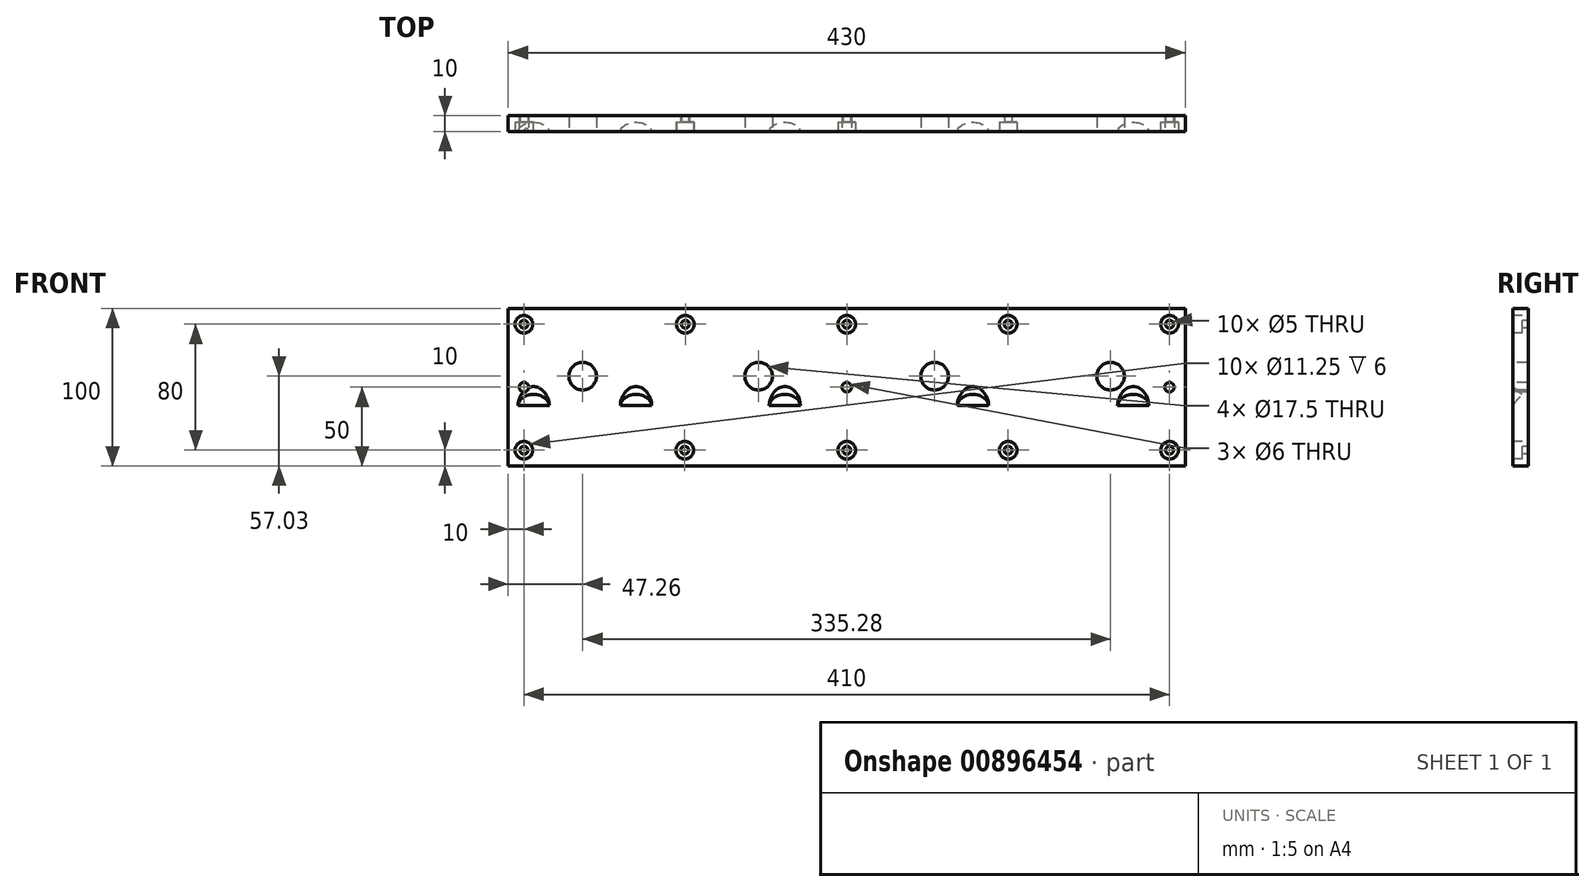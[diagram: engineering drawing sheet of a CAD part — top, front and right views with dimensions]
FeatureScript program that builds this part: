
annotation { "Feature Type Name" : "Feature", "Feature Type Description" : "" }
export const myFeature = defineFeature(function(context is Context, id is Id, definition is map)
    precondition{}
    {
        {
            var Q0;
            Q0=qCreatedBy(makeId("Front.planeOp"),FACE);
            var sketch = newSketch(context, id + "F0", { "sketchPlane" : qUnion([Q0])});
            skLineSegment(sketch, "E0.bottom", {"start": v(0, 0) * mm, "end": v(430, 0) * mm});
            skLineSegment(sketch, "E0.top", {"start": v(0, 100) * mm, "end": v(430, 100) * mm});
            skLineSegment(sketch, "E0.left", {"start": v(0, 0) * mm, "end": v(0, 100) * mm});
            skLineSegment(sketch, "E0.right", {"start": v(430, 0) * mm, "end": v(430, 100) * mm});
            skSolve(sketch);
        }
        {
            var Q0;
            Q0=makeQuery(id+"F0.imprint","IMPRINT",FACE,{"disambiguationData":[TD([[makeQuery(id+"F0.imprint","IMPRINT",EDGE,{"derivedFrom":sQuery(id+"F0.wireOp",EDGE,"E0.bottom")}),1.0]])]});
            extrude(context, id + "F1", {"entities" : qUnion([Q0]), "depth" : 10 * mm, "offsetDistance" : 25 * mm});
        }
        {
            var Q0;
            Q0=makeQuery(id+"F1.opExtrude","CAP_FACE",FACE,{"disambiguationData":[OSD([sQuery(id+"F0.wireOp",EDGE,"E0.bottom"),sQuery(id+"F0.wireOp",EDGE,"E0.top"),sQuery(id+"F0.wireOp",EDGE,"E0.left"),sQuery(id+"F0.wireOp",EDGE,"E0.right")])],"isStart":false});
            var sketch = newSketch(context, id + "F2", { "sketchPlane" : qUnion([Q0])});
            skPoint(sketch, "E1", {"position": v(47.26, 57.03) * mm});
            skPoint(sketch, "E2", {"position": v(159.02, 57.03) * mm});
            skPoint(sketch, "E3", {"position": v(270.78, 57.03) * mm});
            skPoint(sketch, "E4", {"position": v(382.54, 57.03) * mm});
            skPoint(sketch, "E5", {"position": v(10, 10) * mm});
            skPoint(sketch, "E6", {"position": v(112.05, 10) * mm});
            skPoint(sketch, "E7", {"position": v(215, 10) * mm});
            skPoint(sketch, "E8", {"position": v(317.5, 10) * mm});
            skPoint(sketch, "E9", {"position": v(10, 90) * mm});
            skPoint(sketch, "E10", {"position": v(112.5, 90) * mm});
            skPoint(sketch, "E11", {"position": v(215, 90) * mm});
            skPoint(sketch, "E12", {"position": v(317.5, 90) * mm});
            skPoint(sketch, "E13", {"position": v(420, 90) * mm});
            skPoint(sketch, "E14", {"position": v(420, 10) * mm});
            skPoint(sketch, "E15.positionSnap0", {"position": v(0, 50) * mm});
            skPoint(sketch, "E16", {"position": v(215, 50) * mm});
            skPoint(sketch, "E17", {"position": v(420, 50) * mm});
            skPoint(sketch, "E18", {"position": v(10, 50) * mm});
            skSolve(sketch);
        }
        {
            var Q0;
            Q0=sQuery(id+"F2.wireOp",VERTEX,"E1");
            var Q1;
            Q1=sQuery(id+"F2.wireOp",VERTEX,"E2");
            var Q2;
            Q2=sQuery(id+"F2.wireOp",VERTEX,"E3");
            var Q3;
            Q3=sQuery(id+"F2.wireOp",VERTEX,"E4");
            var Q4;
            Q4=makeQuery(id+"F1.opExtrude","SWEPT_BODY",BODY,{"disambiguationData":[OSD([sQuery(id+"F0.wireOp",EDGE,"E0.bottom"),sQuery(id+"F0.wireOp",EDGE,"E0.top"),sQuery(id+"F0.wireOp",EDGE,"E0.left"),sQuery(id+"F0.wireOp",EDGE,"E0.right")])]});
            hole(context, id + "F3", {"style" : HoleStyle.SIMPLE, "endStyle" : HoleEndStyle.THROUGH, "standardTappedOrClearance" : lookupTablePath({ "standard" : "ISO", "engagement" : "75%", "pitch" : "2.5 mm", "size" : "M20", "type" : "Tapped" }), "standardBlindInLast" : lookupTablePath({ "standard" : "ISO", "engagement" : "75%", "pitch" : "2.5 mm", "size" : "M20", "type" : "Tapped" }), "holeDiameter" : 17.5 * mm, "majorDiameter" : 20 * mm, "showTappedDepth" : true, "isTappedThrough" : true, "tappedDepth" : 11.5 * mm, "tapClearance" : 3, "locations" : qUnion([Q0, Q1, Q2, Q3]), "scope" : qUnion([Q4])});
        }
        {
            var Q0;
            Q0=sQuery(id+"F2.wireOp",VERTEX,"E9");
            var Q1;
            Q1=sQuery(id+"F2.wireOp",VERTEX,"E10");
            var Q2;
            Q2=sQuery(id+"F2.wireOp",VERTEX,"E11");
            var Q3;
            Q3=sQuery(id+"F2.wireOp",VERTEX,"E12");
            var Q4;
            Q4=sQuery(id+"F2.wireOp",VERTEX,"E13");
            var Q5;
            Q5=sQuery(id+"F2.wireOp",VERTEX,"E14");
            var Q6;
            Q6=sQuery(id+"F2.wireOp",VERTEX,"E8");
            var Q7;
            Q7=sQuery(id+"F2.wireOp",VERTEX,"E7");
            var Q8;
            Q8=sQuery(id+"F2.wireOp",VERTEX,"E6");
            var Q9;
            Q9=sQuery(id+"F2.wireOp",VERTEX,"E5");
            var Q10;
            Q10=makeQuery(id+"F1.opExtrude","SWEPT_BODY",BODY,{"disambiguationData":[OSD([sQuery(id+"F0.wireOp",EDGE,"E0.bottom"),sQuery(id+"F0.wireOp",EDGE,"E0.top"),sQuery(id+"F0.wireOp",EDGE,"E0.left"),sQuery(id+"F0.wireOp",EDGE,"E0.right")])]});
            hole(context, id + "F4", {"style" : HoleStyle.C_BORE, "endStyle" : HoleEndStyle.THROUGH, "standardTappedOrClearance" : lookupTablePath({ "standard" : "ISO", "engagement" : "75%", "pitch" : "1 mm", "size" : "M6", "type" : "Tapped" }), "standardBlindInLast" : lookupTablePath({ "standard" : "ISO", "engagement" : "75%", "pitch" : "1 mm", "size" : "M6", "type" : "Tapped" }), "holeDiameter" : 5 * mm, "cBoreDiameter" : 11.25 * mm, "cBoreDepth" : 6 * mm, "majorDiameter" : 6 * mm, "showTappedDepth" : true, "isTappedThrough" : true, "tappedDepth" : 11.5 * mm, "tapClearance" : 3, "locations" : qUnion([Q0, Q1, Q2, Q3, Q4, Q5, Q6, Q7, Q8, Q9]), "scope" : qUnion([Q10])});
        }
        {
            var Q0;
            Q0=sQuery(id+"F2.wireOp",VERTEX,"E18");
            var Q1;
            Q1=sQuery(id+"F2.wireOp",VERTEX,"E16");
            var Q2;
            Q2=sQuery(id+"F2.wireOp",VERTEX,"E17");
            var Q3;
            Q3=makeQuery(id+"F1.opExtrude","SWEPT_BODY",BODY,{"disambiguationData":[OSD([sQuery(id+"F0.wireOp",EDGE,"E0.bottom"),sQuery(id+"F0.wireOp",EDGE,"E0.top"),sQuery(id+"F0.wireOp",EDGE,"E0.left"),sQuery(id+"F0.wireOp",EDGE,"E0.right")])]});
            hole(context, id + "F5", {"style" : HoleStyle.SIMPLE, "endStyle" : HoleEndStyle.THROUGH, "standardTappedOrClearance" : lookupTablePath({ "standard" : "ISO", "size" : "6", "type" : "Drilled" }), "standardBlindInLast" : lookupTablePath({ "standard" : "ISO", "size" : "6", "type" : "Drilled" }), "holeDiameter" : 6 * mm, "majorDiameter" : 20 * mm, "isTappedThrough" : true, "tappedDepth" : 11.5 * mm, "tapClearance" : 3, "locations" : qUnion([Q0, Q1, Q2]), "scope" : qUnion([Q3])});
        }
        {
            var Q0;
            Q0=makeQuery(id+"F2.imprint","IMPRINT",FACE,{"disambiguationData":[TD([[makeQuery(id+"F2.imprint","IMPRINT",EDGE,{"derivedFrom":makeQuery(id+"F1.opExtrude","CAP_EDGE",EDGE,{"disambiguationData":[OSD([sQuery(id+"F0.wireOp",EDGE,"E0.bottom")])],"isStart":false})}),1.0]])]});
            var sketch = newSketch(context, id + "F6", { "sketchPlane" : qUnion([Q0])});
            skLineSegment(sketch, "E19", {"start": v(17, 38.5) * mm, "end": v(416.66, 38.5) * mm});
            skSolve(sketch);
        }
        {
            var Q0;
            Q0=sQuery(id+"F6.wireOp",EDGE,"E19");
            cPlane(context, id + "F7", {"entities" : qUnion([Q0]), "cplaneType" : CPlaneType.LINE_ANGLE, "offset" : 25 * mm, "angle" : 40 * degree, "oppositeDirection" : true, "width" : 150 * mm, "height" : 150 * mm});
        }
        {
            var Q0;
            Q0=qCreatedBy(id+"F7.planeOp",FACE);
            var sketch = newSketch(context, id + "F8", { "sketchPlane" : qUnion([Q0])});
            skPoint(sketch, "E20", {"position": v(-16.12, 22.16) * mm});
            skPoint(sketch, "E21", {"position": v(-81.17, 22.16) * mm});
            skPoint(sketch, "E22", {"position": v(-175.68, 22.16) * mm});
            skPoint(sketch, "E23", {"position": v(-295.13, 22.16) * mm});
            skPoint(sketch, "E24", {"position": v(-397, 22.16) * mm});
            skCircle(sketch, "E25", {"center": v(-16.12, 22.16) * mm, "radius": 10 * mm});
            skCircle(sketch, "E26", {"center": v(-81.17, 22.16) * mm, "radius": 10 * mm});
            skCircle(sketch, "E27", {"center": v(-175.68, 22.16) * mm, "radius": 10 * mm});
            skCircle(sketch, "E28", {"center": v(-295.13, 22.16) * mm, "radius": 10 * mm});
            skCircle(sketch, "E29", {"center": v(-397, 22.16) * mm, "radius": 10 * mm});
            skSolve(sketch);
        }
        {
            var Q0;
            Q0 = qSketchRegion(id + "F8", true);
            extrude(context, id + "F9", {"entities" : qUnion([Q0]), "operationType" : NewBodyOperationType.REMOVE, "oppositeDirection" : true, "depth" : 10 * mm, "offsetDistance" : 25 * mm});
        }
    });
